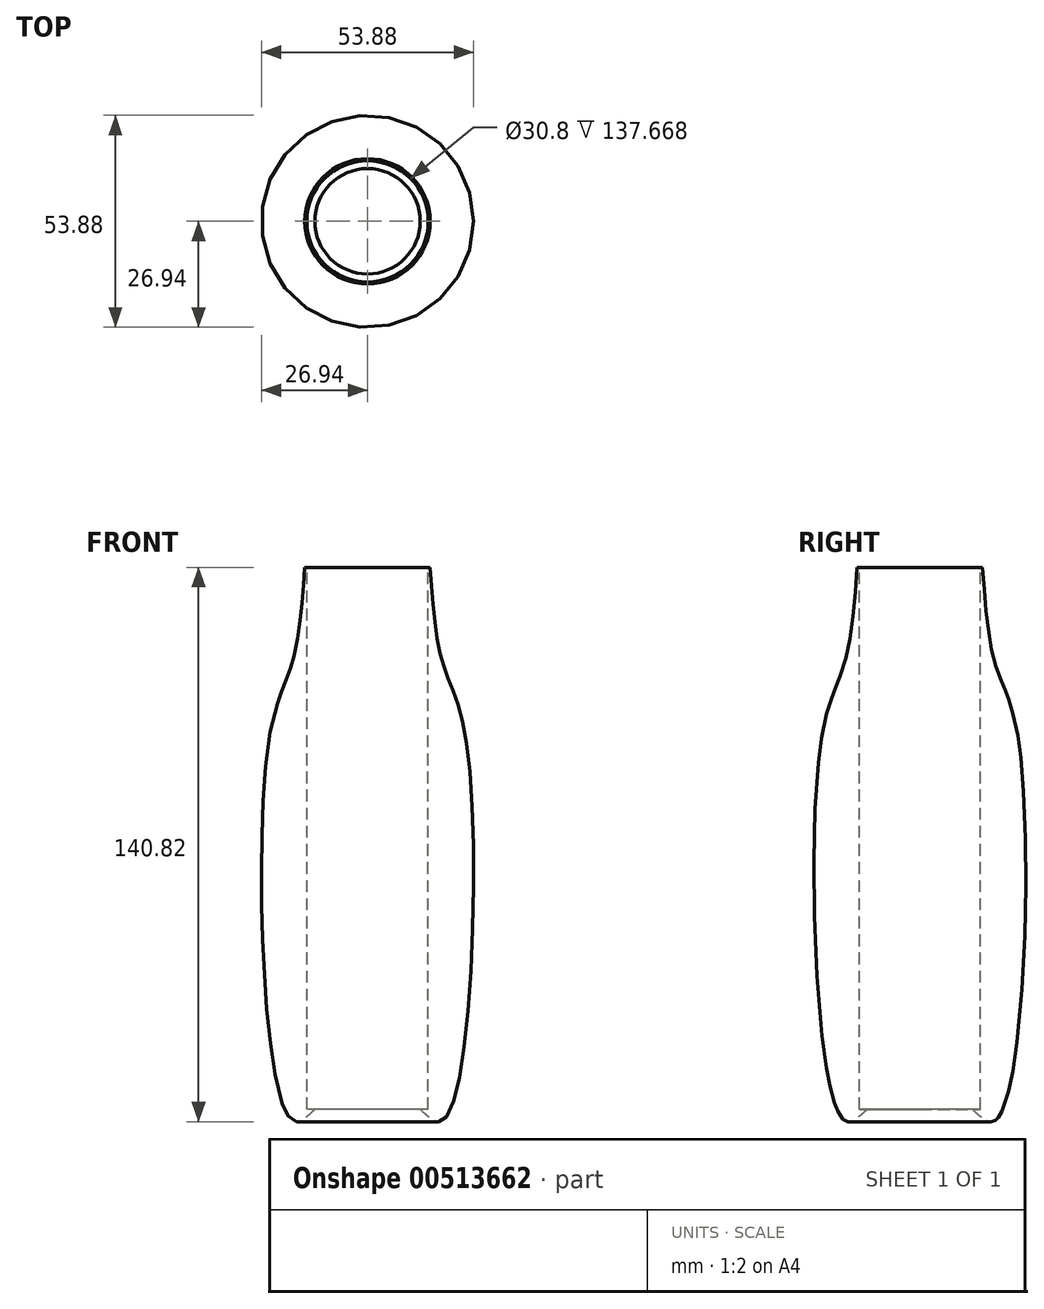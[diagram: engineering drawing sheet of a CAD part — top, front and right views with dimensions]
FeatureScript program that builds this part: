
annotation { "Feature Type Name" : "Feature", "Feature Type Description" : "" }
export const myFeature = defineFeature(function(context is Context, id is Id, definition is map)
    precondition{}
    {
        {
            var Q0;
            Q0=qCreatedBy(makeId("Front.planeOp"),FACE);
            var sketch = newSketch(context, id + "F0", { "sketchPlane" : qUnion([Q0])});
            skFitSpline(sketch, "E0", {"points": [v(0, -68.8) * mm, v(10.25, -70.36) * mm, v(19.14, -75.92) * mm, v(25.45, 18.05) * mm, v(19.1, 40.26) * mm, v(15.93, 64.58) * mm], "startDerivative": vector(84.13, 8.46) * mm, "endDerivative": vector(-10.34, 141.89) * mm});
            skLineSegment(sketch, "E1", {"start": v(15.93, 64.58) * mm, "end": v(0, 64.58) * mm});
            skLineSegment(sketch, "E2", {"start": v(0, 64.58) * mm, "end": v(0, -68.8) * mm});
            skLineSegment(sketch, "E3", {"start": v(0, 77.27) * mm, "end": v(0, -156.43) * mm, "construction": true});
            skSolve(sketch);
        }
        {
            var Q0;
            Q0=makeQuery(id+"F0.imprint","IMPRINT",FACE,{"disambiguationData":[TD([[makeQuery(id+"F0.imprint","IMPRINT",EDGE,{"derivedFrom":sQuery(id+"F0.wireOp",EDGE,"E0")}),1.0]])]});
            var Q1;
            Q1=sQuery(id+"F0.wireOp",EDGE,"E2");
            revolve(context, id + "F1", {"entities" : qUnion([Q0]), "axis" : qUnion([Q1]), "revolveType" : RevolveType.FULL});
        }
        {
            var Q0;
            Q0=makeQuery(id+"F1.opRevolve","SWEPT_FACE",FACE,{"disambiguationData":[OSD([sQuery(id+"F0.wireOp",EDGE,"E1")])]});
            var sketch = newSketch(context, id + "F2", { "sketchPlane" : qUnion([Q0])});
            skCircle(sketch, "E4", {"center": v(0, 0) * mm, "radius": 15.4 * mm});
            skSolve(sketch);
        }
        {
            var Q0;
            Q0=makeQuery(id+"F2.imprint","IMPRINT",FACE,{"disambiguationData":[TD([[makeQuery(id+"F2.imprint","IMPRINT",EDGE,{"derivedFrom":sQuery(id+"F2.wireOp",EDGE,"E4")}),1.0]])]});
            extrude(context, id + "F3", {"entities" : qUnion([Q0]), "operationType" : NewBodyOperationType.REMOVE, "oppositeDirection" : true, "depth" : 137.67 * mm});
        }
    });
